# Revit family: AV150
name_source: partatom
category: Mechanical Equipment
units: mm (PartAtom-declared; Revit-internal decimal feet)

## family parameters
Always vertical = No
Classification = None
Cut with Voids When Loaded = No
Maintain Annotation Orientation = No
OmniClass Number = 23.75.35.17.11
OmniClass Title = Fans for Air Ductwork
Part Type = Breaks Into
Room Calculation Point = No
Round Connector Dimension = Use Diameter
Shared = No
Work Plane-Based = No

## types (1)
- Aventa Silent AVS150
    Apparent Power = 52 VA
    Current = 0 A
    D = 150 mm  [stored 0.492126 ft]
    D1 = 244 mm  [stored 0.800525 ft]
    Dd12 = 3 mm  [stored 0.00984252 ft]
    Dd13 = 4 mm  [stored 0.0131234 ft]
    Dd14 = 28 mm  [stored 0.0918635 ft]
    Dd16 = 45 mm  [stored 0.147638 ft]
    Dd22 = 3 mm  [stored 0.00984252 ft]
    Dd23 = 4 mm  [stored 0.0131234 ft]
    Dd24 = 22 mm  [stored 0.0721785 ft]
    Dd26 = 44 mm  [stored 0.144357 ft]
    Default Elevation = 0 mm  [stored 0 ft]
    Description = Inline mixed-flow fan suitable for domestic and light commercial facilities
    Distribution Box Material = Distribution Box Dark Grey
    Duct Connection Size = 150 mm  [stored 0.492126 ft]
    ElBoxH = 137 mm  [stored 0.449475 ft]
    ElBoxL = 114 mm  [stored 0.374016 ft]
    ElBoxR = 15 mm  [stored 0.0492126 ft]
    ElBoxW = 150 mm  [stored 0.492126 ft]
    Family Version = 1.0
    Fan Material = Metal Black
    Hanger Material = Metal Zinc
    HangerBaseH = 126 mm  [stored 0.413386 ft]
    HangerExtraL = Yes
    HangerH = 126 mm  [stored 0.413386 ft]
    HangerL = 238 mm  [stored 0.78084 ft]
    HangerL1 = 238 mm  [stored 0.78084 ft]
    HangerW = 93 mm  [stored 0.305118 ft]
    L = 580 mm  [stored 1.90289 ft]
    L1 = 25 mm  [stored 0.082021 ft]
    L11 = 163 mm  [stored 0.534777 ft]
    L12 = 8 mm  [stored 0.0262467 ft]
    L13 = 13 mm
    L14 = 21 mm  [stored 0.0688976 ft]
    L15 = 107 mm
    L16 = 8 mm  [stored 0.0262467 ft]
    L17 = 6 mm  [stored 0.019685 ft]
    L2 = 25 mm  [stored 0.082021 ft]
    L21 = 209 mm  [stored 0.685696 ft]
    L22 = 8 mm  [stored 0.0262467 ft]
    L23 = 13 mm
    L24 = 11 mm  [stored 0.0360892 ft]
    L25 = 163 mm  [stored 0.534777 ft]
    L26 = 8 mm  [stored 0.0262467 ft]
    L27 = 6 mm  [stored 0.019685 ft]
    Load Classification = HVAC
    Maintenance Zone Height = 600 mm  [stored 1.9685 ft]
    Maintenance Zone Length = 600 mm  [stored 1.9685 ft]
    Maintenance Zone Length Calc = 600 mm  [stored 1.9685 ft]
    Maintenance Zone Material = Maintenance Zone
    Maintenance Zone Width = 600 mm  [stored 1.9685 ft]
    Manufacturer = Vents
    Maximum Air Flow = 555 m³/h
    Model = Aventa Silent AVS150
    Noise Level at 3 m (dBa) = 33
    Number of Poles = 1
    Power = 52 W
    Power Factor = 1
    Protection rating = IPX4
    R1 = 122 mm  [stored 0.400262 ft]
    RPM (min-1) = 2645
    Transported Air Temperature (°C) = -25...+60
    Type Comments = Inlinefan single speed up to 555m3/h
    URL = https://www.airflow.com
    Voltage = 230 V
    Weight = 6.10 kg

note: [stored X ft] marks values corroborated as IEEE doubles in the binary element streams (Revit-internal decimal feet)

## geometry (parser evidence)
native form markers: Sweep x9
no freeform markers — native parametric forms only
